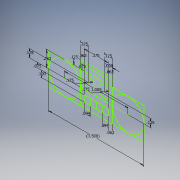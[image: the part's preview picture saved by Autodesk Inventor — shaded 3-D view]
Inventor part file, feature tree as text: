
AUTODESK INVENTOR PART (.ipt)
format: ipt  version: 2016 (Build 200138000, 138)  size: 112,640 bytes
history: native  units: in
note: dims shown in document units (in); Inventor stores cm internally (conversion verified against a paired STEP export)
features: sketch x1
ambient origin geometry x8: Origin, YZ Plane, XZ Plane, XY Plane, X Axis, Y Axis, Z Axis, Center Point
feature tree (1):
  sketch  "Sketch1"  dims[d0=1.0in d1=0.25in d4=0.125in d5=0.075in d7=0.0625in d8=0.0625in d11=0.1in d12=0.075in d13=0.0in d14=0.375in d15=0.0625in d16=0.0938in d17=0.0938in d18=0.175in d19=0.175in d20=0.125in d21=0.125in d22=1.5in d23=0.125in d24=0.125in]
